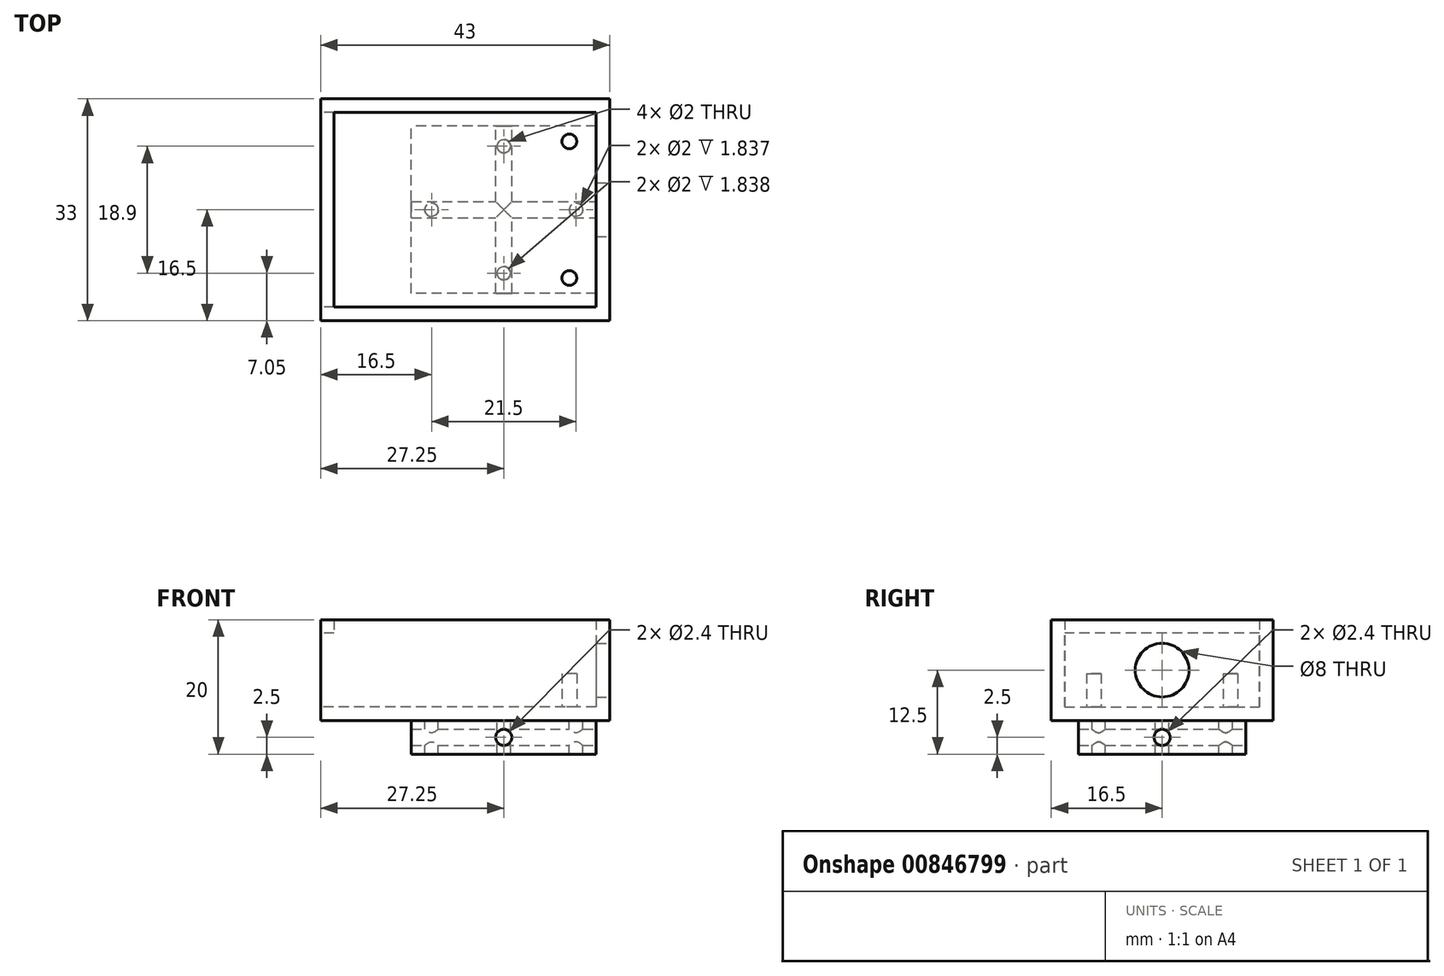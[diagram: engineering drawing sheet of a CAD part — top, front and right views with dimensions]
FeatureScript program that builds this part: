
annotation { "Feature Type Name" : "Feature", "Feature Type Description" : "" }
export const myFeature = defineFeature(function(context is Context, id is Id, definition is map)
    precondition{}
    {
        {
            var Q0;
            Q0=qCreatedBy(makeId("Top.planeOp"),FACE);
            var sketch = newSketch(context, id + "F0", { "sketchPlane" : qUnion([Q0])});
            skLineSegment(sketch, "E0.bottom", {"start": v(19.5, -14.5) * mm, "end": v(-19.5, -14.5) * mm});
            skLineSegment(sketch, "E0.top", {"start": v(19.5, 14.5) * mm, "end": v(-19.5, 14.5) * mm});
            skLineSegment(sketch, "E0.left", {"start": v(19.5, -14.5) * mm, "end": v(19.5, 14.5) * mm});
            skLineSegment(sketch, "E0.right", {"start": v(-19.5, -14.5) * mm, "end": v(-19.5, 14.5) * mm});
            skPoint(sketch, "E0.middle", {"position": v(0, 0) * mm});
            skCircle(sketch, "E1", {"center": v(15.5, 10.16) * mm, "radius": 1.1 * mm});
            skCircle(sketch, "E2", {"center": v(15.5, -10.16) * mm, "radius": 1.1 * mm});
            skLineSegment(sketch, "E3.bottom", {"start": v(21.5, -16.5) * mm, "end": v(-21.5, -16.5) * mm});
            skLineSegment(sketch, "E3.top", {"start": v(21.5, 16.5) * mm, "end": v(-21.5, 16.5) * mm});
            skLineSegment(sketch, "E3.left", {"start": v(21.5, -16.5) * mm, "end": v(21.5, 16.5) * mm});
            skLineSegment(sketch, "E3.right", {"start": v(-21.5, -16.5) * mm, "end": v(-21.5, 16.5) * mm});
            skSolve(sketch);
        }
        {
            var Q0;
            Q0=makeQuery(id+"F0.imprint","IMPRINT",FACE,{"disambiguationData":[TD([[makeQuery(id+"F0.imprint","IMPRINT",EDGE,{"derivedFrom":sQuery(id+"F0.wireOp",EDGE,"E0.bottom")}),1.0]])]});
            extrude(context, id + "F1", {"entities" : qUnion([Q0]), "depth" : 15 * mm, "offsetDistance" : 25 * mm});
        }
        {
            var Q0;
            Q0=makeQuery(id+"F0.imprint","IMPRINT",FACE,{"disambiguationData":[TD([[makeQuery(id+"F0.imprint","IMPRINT",EDGE,{"derivedFrom":sQuery(id+"F0.wireOp",EDGE,"E0.bottom")}),-1.0]])]});
            extrude(context, id + "F2", {"entities" : qUnion([Q0]), "operationType" : NewBodyOperationType.ADD, "depth" : 2 * mm, "offsetDistance" : 25 * mm});
        }
        {
            var Q0;
            Q0=makeQuery(id+"F0.imprint","IMPRINT",FACE,{"disambiguationData":[TD([[makeQuery(id+"F0.imprint","IMPRINT",EDGE,{"derivedFrom":sQuery(id+"F0.wireOp",EDGE,"E2")}),1.0]])]});
            var Q1;
            Q1=makeQuery(id+"F0.imprint","IMPRINT",FACE,{"disambiguationData":[TD([[makeQuery(id+"F0.imprint","IMPRINT",EDGE,{"derivedFrom":sQuery(id+"F0.wireOp",EDGE,"E1")}),1.0]])]});
            extrude(context, id + "F3", {"entities" : qUnion([Q0, Q1]), "operationType" : NewBodyOperationType.ADD, "depth" : 7 * mm, "offsetDistance" : 25 * mm});
        }
        {
            var Q0;
            Q0=makeQuery(id+"F1.opExtrude","SWEPT_FACE",FACE,{"disambiguationData":[OSD([sQuery(id+"F0.wireOp",EDGE,"E3.left")])]});
            var sketch = newSketch(context, id + "F4", { "sketchPlane" : qUnion([Q0])});
            skCircle(sketch, "E4", {"center": v(0, 7.5) * mm, "radius": 4 * mm});
            skPoint(sketch, "E4.centerSnap0", {"position": v(0, 15) * mm});
            skPoint(sketch, "E4.centerSnap1", {"position": v(-16.5, 7.5) * mm});
            skSolve(sketch);
        }
        {
            var Q0;
            Q0=makeQuery(id+"F4.imprint","IMPRINT",FACE,{"disambiguationData":[TD([[makeQuery(id+"F4.imprint","IMPRINT",EDGE,{"derivedFrom":sQuery(id+"F4.wireOp",EDGE,"E4")}),1.0]])]});
            extrude(context, id + "F5", {"entities" : qUnion([Q0]), "operationType" : NewBodyOperationType.REMOVE, "endBound" : BoundingType.UP_TO_NEXT, "oppositeDirection" : true, "depth" : 25 * mm, "offsetDistance" : 25 * mm});
        }
        {
            var Q0;
            Q0=makeQuery(id+"F1.opExtrude","SWEPT_FACE",FACE,{"disambiguationData":[OSD([sQuery(id+"F0.wireOp",EDGE,"E3.right")])]});
            var sketch = newSketch(context, id + "F6", { "sketchPlane" : qUnion([Q0])});
            skLineSegment(sketch, "E5.bottom", {"start": v(14.5, 2) * mm, "end": v(-14.5, 2) * mm});
            skLineSegment(sketch, "E5.top", {"start": v(14.5, 13) * mm, "end": v(-14.5, 13) * mm});
            skLineSegment(sketch, "E5.left", {"start": v(14.5, 2) * mm, "end": v(14.5, 13) * mm});
            skLineSegment(sketch, "E5.right", {"start": v(-14.5, 2) * mm, "end": v(-14.5, 13) * mm});
            skPoint(sketch, "E5.middle", {"position": v(0, 7.5) * mm});
            skPoint(sketch, "E5.middle.positionSnap0", {"position": v(-16.5, 7.5) * mm});
            skPoint(sketch, "E5.middle.positionSnap1", {"position": v(0, 15) * mm});
            skPoint(sketch, "E5.centerSnap0", {"position": v(-16.5, 7.5) * mm});
            skPoint(sketch, "E5.centerSnap1", {"position": v(0, 15) * mm});
            skSolve(sketch);
        }
        {
            var Q0;
            Q0=makeQuery(id+"F6.imprint","IMPRINT",FACE,{"disambiguationData":[TD([[makeQuery(id+"F6.imprint","IMPRINT",EDGE,{"derivedFrom":sQuery(id+"F6.wireOp",EDGE,"E5.bottom")}),-1.0]])]});
            extrude(context, id + "F7", {"entities" : qUnion([Q0]), "operationType" : NewBodyOperationType.REMOVE, "endBound" : BoundingType.UP_TO_NEXT, "oppositeDirection" : true, "depth" : 25 * mm, "offsetDistance" : 25 * mm});
        }
        {
            var Q0;
            {var subQ0=sQuery(id+"F0.wireOp",EDGE,"E2");var subQ1=sQuery(id+"F0.wireOp",EDGE,"E1");var subQ2=sQuery(id+"F0.wireOp",EDGE,"E0.right");var subQ3=sQuery(id+"F0.wireOp",EDGE,"E0.left");var subQ4=sQuery(id+"F0.wireOp",EDGE,"E0.top");var subQ5=sQuery(id+"F0.wireOp",EDGE,"E0.bottom");Q0=makeQuery(id+"F3.boolean.opBoolean","MERGE",FACE,{"derivedFrom":[makeQuery(id+"F2.boolean.opBoolean","MERGE",FACE,{"derivedFrom":[makeQuery(id+"F1.opExtrude","CAP_FACE",FACE,{"disambiguationData":[OSD([subQ5,subQ4,subQ3,subQ2,sQuery(id+"F0.wireOp",EDGE,"E3.bottom"),sQuery(id+"F0.wireOp",EDGE,"E3.top"),sQuery(id+"F0.wireOp",EDGE,"E3.left"),sQuery(id+"F0.wireOp",EDGE,"E3.right")])],"isStart":true}),makeQuery(id+"F2.opExtrude","CAP_FACE",FACE,{"disambiguationData":[OSD([subQ5,subQ4,subQ3,subQ2,subQ1,subQ0])],"isStart":true})]}),makeQuery(id+"F3.opExtrude","CAP_FACE",FACE,{"disambiguationData":[OSD([subQ1])],"isStart":true}),makeQuery(id+"F3.opExtrude","CAP_FACE",FACE,{"disambiguationData":[OSD([subQ0])],"isStart":true})]});}
            var sketch = newSketch(context, id + "F8", { "sketchPlane" : qUnion([Q0])});
            skLineSegment(sketch, "E6.bottom", {"start": v(19.5, 12.45) * mm, "end": v(-8, 12.45) * mm});
            skLineSegment(sketch, "E6.top", {"start": v(19.5, -12.45) * mm, "end": v(-8, -12.45) * mm});
            skLineSegment(sketch, "E6.left", {"start": v(19.5, 12.45) * mm, "end": v(19.5, -12.45) * mm});
            skLineSegment(sketch, "E6.right", {"start": v(-8, 12.45) * mm, "end": v(-8, -12.45) * mm});
            skPoint(sketch, "E6.middle", {"position": v(0, 0) * mm});
            skLineSegment(sketch, "E7.bottom", {"start": v(16.5, 9.45) * mm, "end": v(-5, 9.45) * mm});
            skLineSegment(sketch, "E7.top", {"start": v(16.5, -9.45) * mm, "end": v(-5, -9.45) * mm});
            skLineSegment(sketch, "E7.left", {"start": v(16.5, 9.45) * mm, "end": v(16.5, -9.45) * mm});
            skLineSegment(sketch, "E7.right", {"start": v(-5, 9.45) * mm, "end": v(-5, -9.45) * mm});
            skCircle(sketch, "E8", {"center": v(5.75, -9.45) * mm, "radius": 1 * mm});
            skCircle(sketch, "E9", {"center": v(16.5, 0) * mm, "radius": 1 * mm});
            skCircle(sketch, "E10", {"center": v(5.75, 9.45) * mm, "radius": 1 * mm});
            skCircle(sketch, "E11", {"center": v(-5, 0) * mm, "radius": 1 * mm});
            skSolve(sketch);
        }
        {
            var Q0;
            Q0=makeQuery(id+"F8.imprint","IMPRINT",FACE,{"disambiguationData":[TD([[makeQuery(id+"F8.imprint","IMPRINT",EDGE,{"derivedFrom":sQuery(id+"F8.wireOp",EDGE,"E6.bottom")}),1.0]])]});
            var Q1;
            {var subQ0=sQuery(id+"F8.wireOp",EDGE,"E9");var subQ1=sQuery(id+"F8.wireOp",EDGE,"E7.left");var subQ2=makeQuery(id+"F8.imprint","INTERSECT",VERTEX,{"disambiguationData":[OD(0.0)],"derivedFrom":[subQ1,subQ0]});Q1=makeQuery(id+"F8.imprint","IMPRINT",FACE,{"disambiguationData":[TD([[makeQuery(id+"F8.imprint","IMPRINT",EDGE,{"disambiguationData":[TD([[subQ2,-1.0]])],"derivedFrom":subQ1}),1.0]])]});}
            var Q2;
            {var subQ0=sQuery(id+"F8.wireOp",EDGE,"E9");var subQ1=sQuery(id+"F8.wireOp",EDGE,"E7.left");var subQ2=makeQuery(id+"F8.imprint","INTERSECT",VERTEX,{"disambiguationData":[OD(0.0)],"derivedFrom":[subQ1,subQ0]});Q2=makeQuery(id+"F8.imprint","IMPRINT",FACE,{"disambiguationData":[TD([[makeQuery(id+"F8.imprint","IMPRINT",EDGE,{"disambiguationData":[TD([[subQ2,-1.0]])],"derivedFrom":subQ1}),-1.0]])]});}
            var Q3;
            {var subQ0=sQuery(id+"F8.wireOp",EDGE,"E8");var subQ1=sQuery(id+"F8.wireOp",EDGE,"E7.top");var subQ2=makeQuery(id+"F8.imprint","INTERSECT",VERTEX,{"disambiguationData":[OD(0.0)],"derivedFrom":[subQ1,subQ0]});Q3=makeQuery(id+"F8.imprint","IMPRINT",FACE,{"disambiguationData":[TD([[makeQuery(id+"F8.imprint","IMPRINT",EDGE,{"disambiguationData":[TD([[subQ2,-1.0]])],"derivedFrom":subQ1}),-1.0]])]});}
            var Q4;
            {var subQ0=sQuery(id+"F8.wireOp",EDGE,"E8");var subQ1=sQuery(id+"F8.wireOp",EDGE,"E7.top");var subQ2=makeQuery(id+"F8.imprint","INTERSECT",VERTEX,{"disambiguationData":[OD(0.0)],"derivedFrom":[subQ1,subQ0]});Q4=makeQuery(id+"F8.imprint","IMPRINT",FACE,{"disambiguationData":[TD([[makeQuery(id+"F8.imprint","IMPRINT",EDGE,{"disambiguationData":[TD([[subQ2,-1.0]])],"derivedFrom":subQ1}),1.0]])]});}
            var Q5;
            {var subQ0=sQuery(id+"F8.wireOp",EDGE,"E10");var subQ1=sQuery(id+"F8.wireOp",EDGE,"E7.bottom");var subQ2=makeQuery(id+"F8.imprint","INTERSECT",VERTEX,{"disambiguationData":[OD(0.0)],"derivedFrom":[subQ1,subQ0]});Q5=makeQuery(id+"F8.imprint","IMPRINT",FACE,{"disambiguationData":[TD([[makeQuery(id+"F8.imprint","IMPRINT",EDGE,{"disambiguationData":[TD([[subQ2,-1.0]])],"derivedFrom":subQ1}),1.0]])]});}
            var Q6;
            {var subQ0=sQuery(id+"F8.wireOp",EDGE,"E10");var subQ1=sQuery(id+"F8.wireOp",EDGE,"E7.bottom");var subQ2=makeQuery(id+"F8.imprint","INTERSECT",VERTEX,{"disambiguationData":[OD(0.0)],"derivedFrom":[subQ1,subQ0]});Q6=makeQuery(id+"F8.imprint","IMPRINT",FACE,{"disambiguationData":[TD([[makeQuery(id+"F8.imprint","IMPRINT",EDGE,{"disambiguationData":[TD([[subQ2,-1.0]])],"derivedFrom":subQ1}),-1.0]])]});}
            var Q7;
            {var subQ0=sQuery(id+"F8.wireOp",EDGE,"E11");var subQ1=sQuery(id+"F8.wireOp",EDGE,"E7.right");var subQ2=makeQuery(id+"F8.imprint","INTERSECT",VERTEX,{"disambiguationData":[OD(0.0)],"derivedFrom":[subQ1,subQ0]});Q7=makeQuery(id+"F8.imprint","IMPRINT",FACE,{"disambiguationData":[TD([[makeQuery(id+"F8.imprint","IMPRINT",EDGE,{"disambiguationData":[TD([[subQ2,-1.0]])],"derivedFrom":subQ1}),1.0]])]});}
            var Q8;
            {var subQ0=sQuery(id+"F8.wireOp",EDGE,"E11");var subQ1=sQuery(id+"F8.wireOp",EDGE,"E7.right");var subQ2=makeQuery(id+"F8.imprint","INTERSECT",VERTEX,{"disambiguationData":[OD(0.0)],"derivedFrom":[subQ1,subQ0]});Q8=makeQuery(id+"F8.imprint","IMPRINT",FACE,{"disambiguationData":[TD([[makeQuery(id+"F8.imprint","IMPRINT",EDGE,{"disambiguationData":[TD([[subQ2,-1.0]])],"derivedFrom":subQ1}),-1.0]])]});}
            extrude(context, id + "F9", {"entities" : qUnion([Q0, Q1, Q2, Q3, Q4, Q5, Q6, Q7, Q8]), "operationType" : NewBodyOperationType.ADD, "depth" : 5 * mm, "offsetDistance" : 25 * mm});
        }
        {
            var Q0;
            Q0=makeQuery(id+"F9.opExtrude","SWEPT_FACE",FACE,{"disambiguationData":[OSD([sQuery(id+"F8.wireOp",EDGE,"E6.left")])]});
            var sketch = newSketch(context, id + "F10", { "sketchPlane" : qUnion([Q0])});
            skPoint(sketch, "E12", {"position": v(0, -2.5) * mm});
            skPoint(sketch, "E12.positionSnap0", {"position": v(0, -5) * mm});
            skPoint(sketch, "E12.positionSnap1", {"position": v(-12.45, -2.5) * mm});
            skSolve(sketch);
        }
        {
            var Q0;
            Q0=sQuery(id+"F10.wireOp",VERTEX,"E12");
            var Q1;
            Q1=makeQuery(id+"F1.opExtrude","SWEPT_BODY",BODY,{"disambiguationData":[OSD([sQuery(id+"F0.wireOp",EDGE,"E0.bottom"),sQuery(id+"F0.wireOp",EDGE,"E0.top"),sQuery(id+"F0.wireOp",EDGE,"E0.left"),sQuery(id+"F0.wireOp",EDGE,"E0.right"),sQuery(id+"F0.wireOp",EDGE,"E3.bottom"),sQuery(id+"F0.wireOp",EDGE,"E3.top"),sQuery(id+"F0.wireOp",EDGE,"E3.left"),sQuery(id+"F0.wireOp",EDGE,"E3.right")])]});
            hole(context, id + "F11", {"style" : HoleStyle.SIMPLE, "endStyle" : HoleEndStyle.THROUGH, "holeDiameter" : 2.4 * mm, "majorDiameter" : 5 * mm, "isTappedThrough" : true, "tappedDepth" : 12 * mm, "tapClearance" : 3, "locations" : qUnion([Q0]), "scope" : qUnion([Q1])});
        }
        {
            var Q0;
            Q0=makeQuery(id+"F9.opExtrude","SWEPT_FACE",FACE,{"disambiguationData":[OSD([sQuery(id+"F8.wireOp",EDGE,"E6.top")])]});
            var sketch = newSketch(context, id + "F12", { "sketchPlane" : qUnion([Q0])});
            skPoint(sketch, "E13", {"position": v(-5.75, -2.5) * mm});
            skPoint(sketch, "E13.positionSnap0", {"position": v(-5.75, -5) * mm});
            skPoint(sketch, "E13.positionSnap1", {"position": v(-19.5, -2.5) * mm});
            skSolve(sketch);
        }
        {
            var Q0;
            Q0=sQuery(id+"F12.wireOp",VERTEX,"E13");
            var Q1;
            Q1=makeQuery(id+"F1.opExtrude","SWEPT_BODY",BODY,{"disambiguationData":[OSD([sQuery(id+"F0.wireOp",EDGE,"E0.bottom"),sQuery(id+"F0.wireOp",EDGE,"E0.top"),sQuery(id+"F0.wireOp",EDGE,"E0.left"),sQuery(id+"F0.wireOp",EDGE,"E0.right"),sQuery(id+"F0.wireOp",EDGE,"E3.bottom"),sQuery(id+"F0.wireOp",EDGE,"E3.top"),sQuery(id+"F0.wireOp",EDGE,"E3.left"),sQuery(id+"F0.wireOp",EDGE,"E3.right")])]});
            hole(context, id + "F13", {"style" : HoleStyle.SIMPLE, "endStyle" : HoleEndStyle.THROUGH, "holeDiameter" : 2.4 * mm, "majorDiameter" : 5 * mm, "isTappedThrough" : true, "tappedDepth" : 12 * mm, "tapClearance" : 3, "locations" : qUnion([Q0]), "scope" : qUnion([Q1])});
        }
    });
